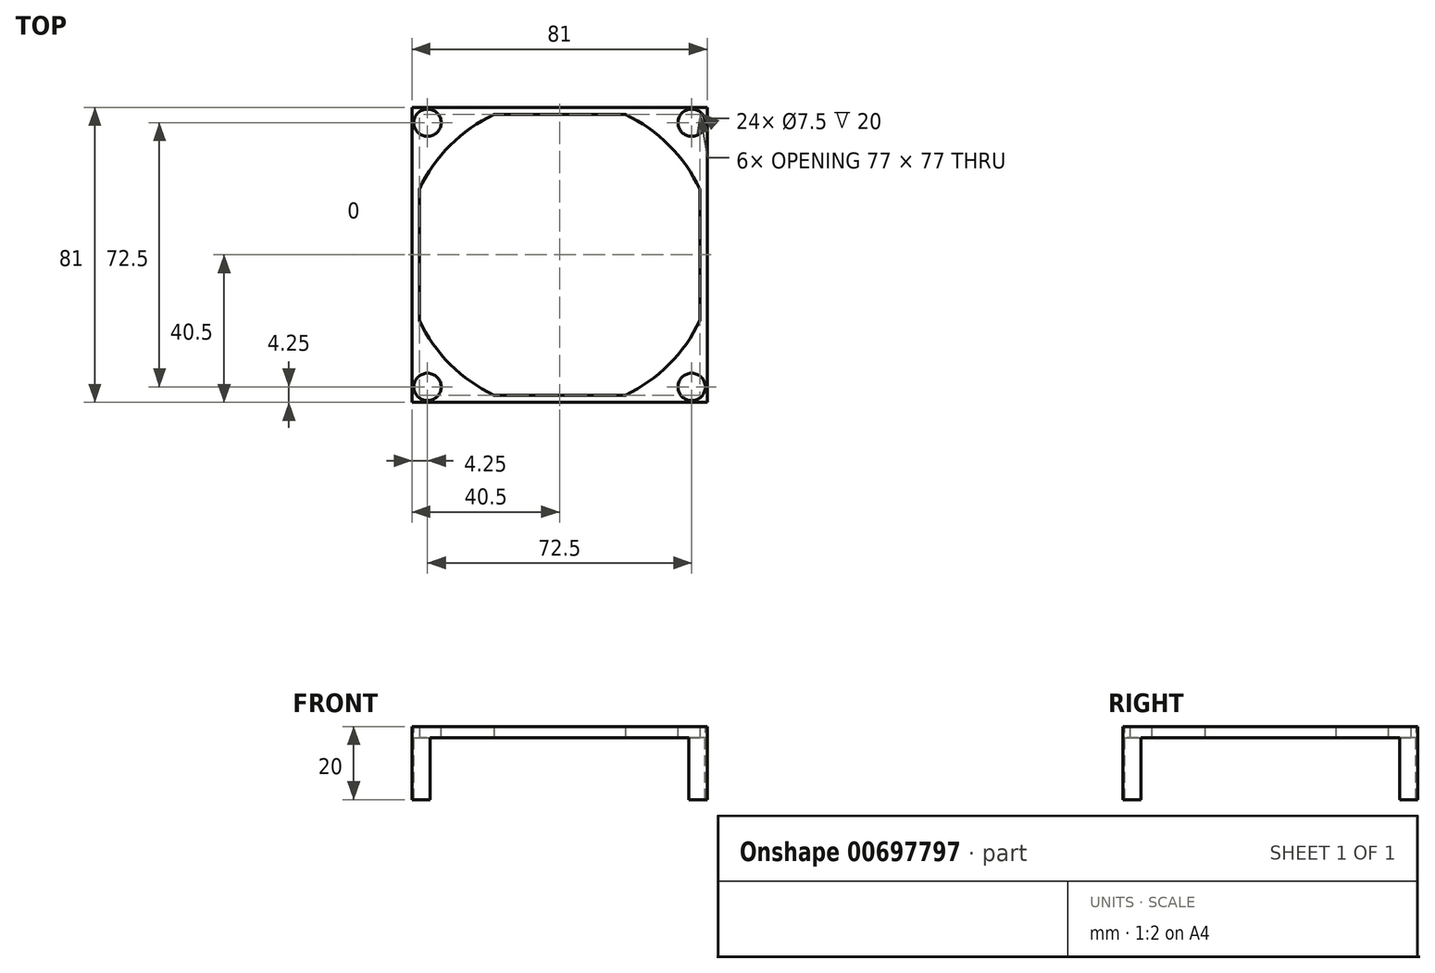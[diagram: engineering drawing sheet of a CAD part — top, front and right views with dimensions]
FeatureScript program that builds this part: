
annotation { "Feature Type Name" : "Feature", "Feature Type Description" : "" }
export const myFeature = defineFeature(function(context is Context, id is Id, definition is map)
    precondition{}
    {
        {
            var Q0;
            Q0=qCreatedBy(makeId("Top.planeOp"),FACE);
            var sketch = newSketch(context, id + "F0", { "sketchPlane" : qUnion([Q0])});
            skArc(sketch, "E0", {"start": v(-18, 38.5) * mm, "mid": v(-30.05, 30.05) * mm, "end": v(-38.5, 18) * mm});
            skLineSegment(sketch, "E1.bottom", {"start": v(-40.5, 40.5) * mm, "end": v(40.5, 40.5) * mm});
            skLineSegment(sketch, "E1.top", {"start": v(-40.5, -40.5) * mm, "end": v(40.5, -40.5) * mm});
            skLineSegment(sketch, "E1.left", {"start": v(-40.5, 40.5) * mm, "end": v(-40.5, -40.5) * mm});
            skLineSegment(sketch, "E1.right", {"start": v(40.5, 40.5) * mm, "end": v(40.5, -40.5) * mm});
            skLineSegment(sketch, "E2", {"start": v(0, 72.48) * mm, "end": v(0, -70.87) * mm, "construction": true});
            skLineSegment(sketch, "E3", {"start": v(-65.97, 0) * mm, "end": v(72.98, 0) * mm, "construction": true});
            skArc(sketch, "E4.trimOffspring", {"start": v(38.5, 18) * mm, "mid": v(30.05, 30.05) * mm, "end": v(18, 38.5) * mm});
            skArc(sketch, "E5.trimOffspring", {"start": v(18, -38.5) * mm, "mid": v(30.05, -30.05) * mm, "end": v(38.5, -18) * mm});
            skArc(sketch, "E6.trimOffspring", {"start": v(-38.5, -18) * mm, "mid": v(-30.05, -30.05) * mm, "end": v(-18, -38.5) * mm});
            skLineSegment(sketch, "E7", {"start": v(-18, 38.5) * mm, "end": v(18, 38.5) * mm});
            skLineSegment(sketch, "E8", {"start": v(-38.5, 18) * mm, "end": v(-38.5, -18) * mm});
            skLineSegment(sketch, "E9", {"start": v(-18, -38.5) * mm, "end": v(18, -38.5) * mm});
            skLineSegment(sketch, "E10", {"start": v(38.5, -18) * mm, "end": v(38.5, 18) * mm});
            skSolve(sketch);
        }
        {
            var Q0;
            Q0 = qSketchRegion(id + "F0", true);
            extrude(context, id + "F1", {"entities" : qUnion([Q0]), "depth" : 20 * mm, "offsetDistance" : 25 * mm});
        }
        {
            var Q0;
            Q0=makeQuery(id+"F1.opExtrude","SWEPT_FACE",FACE,{"disambiguationData":[OSD([sQuery(id+"F0.wireOp",EDGE,"E1.top")])]});
            var sketch = newSketch(context, id + "F2", { "sketchPlane" : qUnion([Q0])});
            skLineSegment(sketch, "E11.bottom", {"start": v(-35.5, 17) * mm, "end": v(35.5, 17) * mm});
            skLineSegment(sketch, "E11.top", {"start": v(-35.5, -3.8) * mm, "end": v(35.5, -3.8) * mm});
            skLineSegment(sketch, "E11.left", {"start": v(-35.5, 17) * mm, "end": v(-35.5, -3.8) * mm});
            skLineSegment(sketch, "E11.right", {"start": v(35.5, 17) * mm, "end": v(35.5, -3.8) * mm});
            skLineSegment(sketch, "E12", {"start": v(0, 44.54) * mm, "end": v(0, -29.46) * mm, "construction": true});
            skSolve(sketch);
        }
        {
            var Q0;
            Q0 = qSketchRegion(id + "F2", true);
            extrude(context, id + "F3", {"entities" : qUnion([Q0]), "operationType" : NewBodyOperationType.REMOVE, "endBound" : BoundingType.THROUGH_ALL, "oppositeDirection" : true, "depth" : 25 * mm, "offsetDistance" : 25 * mm});
        }
        {
            var Q0;
            Q0=makeQuery(id+"F1.opExtrude","SWEPT_FACE",FACE,{"disambiguationData":[OSD([sQuery(id+"F0.wireOp",EDGE,"E1.left")])]});
            var sketch = newSketch(context, id + "F4", { "sketchPlane" : qUnion([Q0])});
            skLineSegment(sketch, "E13.bottom", {"start": v(-35.5, -12.6) * mm, "end": v(35.5, -12.6) * mm});
            skLineSegment(sketch, "E13.top", {"start": v(-35.5, 17) * mm, "end": v(35.5, 17) * mm});
            skLineSegment(sketch, "E13.left", {"start": v(-35.5, -12.6) * mm, "end": v(-35.5, 17) * mm});
            skLineSegment(sketch, "E13.right", {"start": v(35.5, -12.6) * mm, "end": v(35.5, 17) * mm});
            skLineSegment(sketch, "E14", {"start": v(0, 52.91) * mm, "end": v(0, -50.02) * mm, "construction": true});
            skSolve(sketch);
        }
        {
            var Q0;
            Q0 = qSketchRegion(id + "F4", true);
            extrude(context, id + "F5", {"entities" : qUnion([Q0]), "operationType" : NewBodyOperationType.REMOVE, "endBound" : BoundingType.THROUGH_ALL, "oppositeDirection" : true, "depth" : 25 * mm, "offsetDistance" : 25 * mm});
        }
        {
            var Q0;
            Q0=makeQuery(id+"F1.opExtrude","CAP_FACE",FACE,{"disambiguationData":[OSD([sQuery(id+"F0.wireOp",EDGE,"E0"),sQuery(id+"F0.wireOp",EDGE,"E1.bottom"),sQuery(id+"F0.wireOp",EDGE,"E1.top"),sQuery(id+"F0.wireOp",EDGE,"E1.left"),sQuery(id+"F0.wireOp",EDGE,"E1.right"),sQuery(id+"F0.wireOp",EDGE,"E4.trimOffspring"),sQuery(id+"F0.wireOp",EDGE,"E5.trimOffspring"),sQuery(id+"F0.wireOp",EDGE,"E6.trimOffspring"),sQuery(id+"F0.wireOp",EDGE,"E7"),sQuery(id+"F0.wireOp",EDGE,"E8"),sQuery(id+"F0.wireOp",EDGE,"E9"),sQuery(id+"F0.wireOp",EDGE,"E10")])],"isStart":false});
            var sketch = newSketch(context, id + "F6", { "sketchPlane" : qUnion([Q0])});
            skCircle(sketch, "E15", {"center": v(-36.25, 36.25) * mm, "radius": 3.75 * mm});
            skCircle(sketch, "E16", {"center": v(36.25, 36.25) * mm, "radius": 3.75 * mm});
            skLineSegment(sketch, "E17", {"start": v(-100.66, 0) * mm, "end": v(61.07, 0) * mm, "construction": true});
            skCircle(sketch, "E18", {"center": v(-36.25, -36.25) * mm, "radius": 3.75 * mm});
            skCircle(sketch, "E19", {"center": v(36.25, -36.25) * mm, "radius": 3.75 * mm});
            skSolve(sketch);
        }
        {
            var Q0;
            Q0 = qSketchRegion(id + "F6", true);
            extrude(context, id + "F7", {"entities" : qUnion([Q0]), "operationType" : NewBodyOperationType.REMOVE, "endBound" : BoundingType.THROUGH_ALL, "oppositeDirection" : true, "depth" : 25 * mm, "offsetDistance" : 25 * mm});
        }
    });
